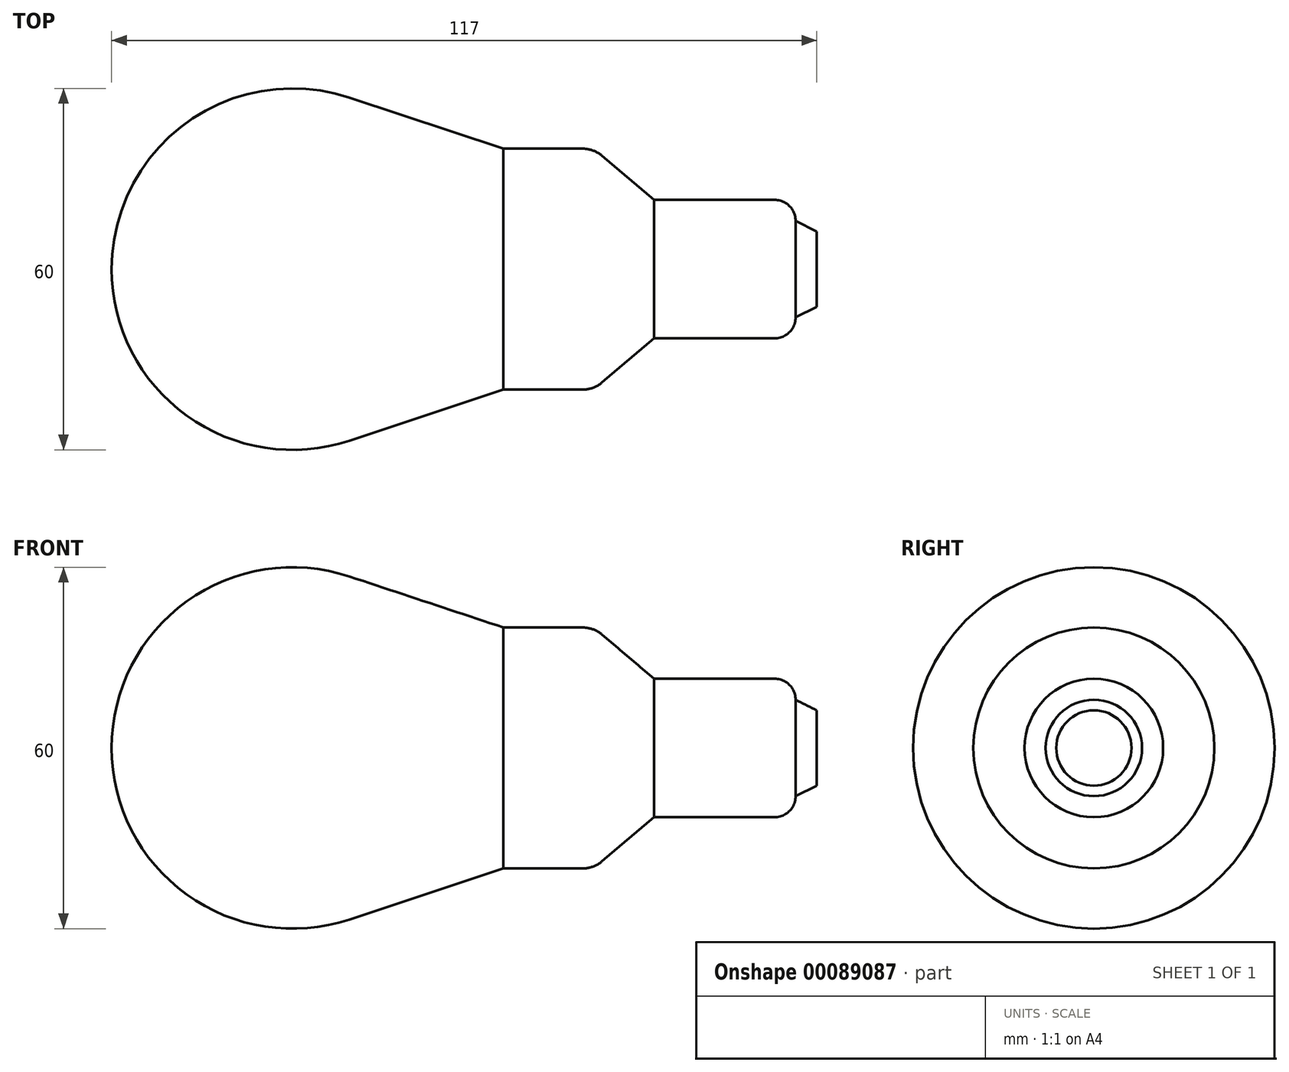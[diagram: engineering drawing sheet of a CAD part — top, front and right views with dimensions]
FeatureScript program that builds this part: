
annotation { "Feature Type Name" : "Feature", "Feature Type Description" : "" }
export const myFeature = defineFeature(function(context is Context, id is Id, definition is map)
    precondition{}
    {
        {
            var Q0;
            Q0=qCreatedBy(makeId("Top.planeOp"),FACE);
            var sketch = newSketch(context, id + "F0", { "sketchPlane" : qUnion([Q0])});
            skLineSegment(sketch, "E0", {"start": v(0, 0) * mm, "end": v(35, 0) * mm, "construction": true});
            skLineSegment(sketch, "E1", {"start": v(35, 0) * mm, "end": v(35, 20) * mm, "construction": true});
            skLineSegment(sketch, "E2", {"start": v(35, 20) * mm, "end": v(9.44, 28.48) * mm});
            skLineSegment(sketch, "E3", {"start": v(35, 20) * mm, "end": v(48.16, 20) * mm});
            skLineSegment(sketch, "E4", {"start": v(35, 0) * mm, "end": v(50, 0) * mm, "construction": true});
            skLineSegment(sketch, "E5", {"start": v(50, 0) * mm, "end": v(60, 0) * mm, "construction": true});
            skLineSegment(sketch, "E6", {"start": v(51.4, 18.8) * mm, "end": v(60, 11.5) * mm});
            skLineSegment(sketch, "E7", {"start": v(0, 0) * mm, "end": v(-30, 0) * mm, "construction": true});
            skArc(sketch, "E8", {"start": v(-30, 0) * mm, "mid": v(-17.56, 24.32) * mm, "end": v(9.44, 28.48) * mm});
            skLineSegment(sketch, "E9", {"start": v(60, 0) * mm, "end": v(80, 0) * mm, "construction": true});
            skLineSegment(sketch, "E10", {"start": v(60, 11.5) * mm, "end": v(80, 11.5) * mm});
            skLineSegment(sketch, "E11", {"start": v(80, 11.5) * mm, "end": v(80, 11.5) * mm});
            skLineSegment(sketch, "E12", {"start": v(83.5, 8) * mm, "end": v(83.5, 8) * mm});
            skPoint(sketch, "E13.visualSharp", {"position": v(83.5, 11.5) * mm});
            skArc(sketch, "E13.filletArc", {"start": v(83.5, 8) * mm, "mid": v(82.47, 10.47) * mm, "end": v(80, 11.5) * mm});
            skLineSegment(sketch, "E14", {"start": v(83.5, 8) * mm, "end": v(87, 6.25) * mm});
            skLineSegment(sketch, "E15", {"start": v(87, 6.25) * mm, "end": v(87, 0) * mm});
            skLineSegment(sketch, "E16", {"start": v(87, 0) * mm, "end": v(-30, 0) * mm});
            skPoint(sketch, "E17.visualSharp", {"position": v(50, 20) * mm});
            skArc(sketch, "E17.filletArc", {"start": v(51.4, 18.8) * mm, "mid": v(49.89, 19.7) * mm, "end": v(48.16, 20) * mm});
            skSolve(sketch);
        }
        {
            var Q0;
            Q0=makeQuery(id+"F0.imprint","IMPRINT",FACE,{"disambiguationData":[TD([[makeQuery(id+"F0.imprint","IMPRINT",EDGE,{"derivedFrom":sQuery(id+"F0.wireOp",EDGE,"E2")}),1.0]])]});
            var Q1;
            Q1=sQuery(id+"F0.wireOp",EDGE,"E0");
            revolve(context, id + "F1", {"entities" : qUnion([Q0]), "axis" : qUnion([Q1]), "revolveType" : RevolveType.FULL});
        }
    });
